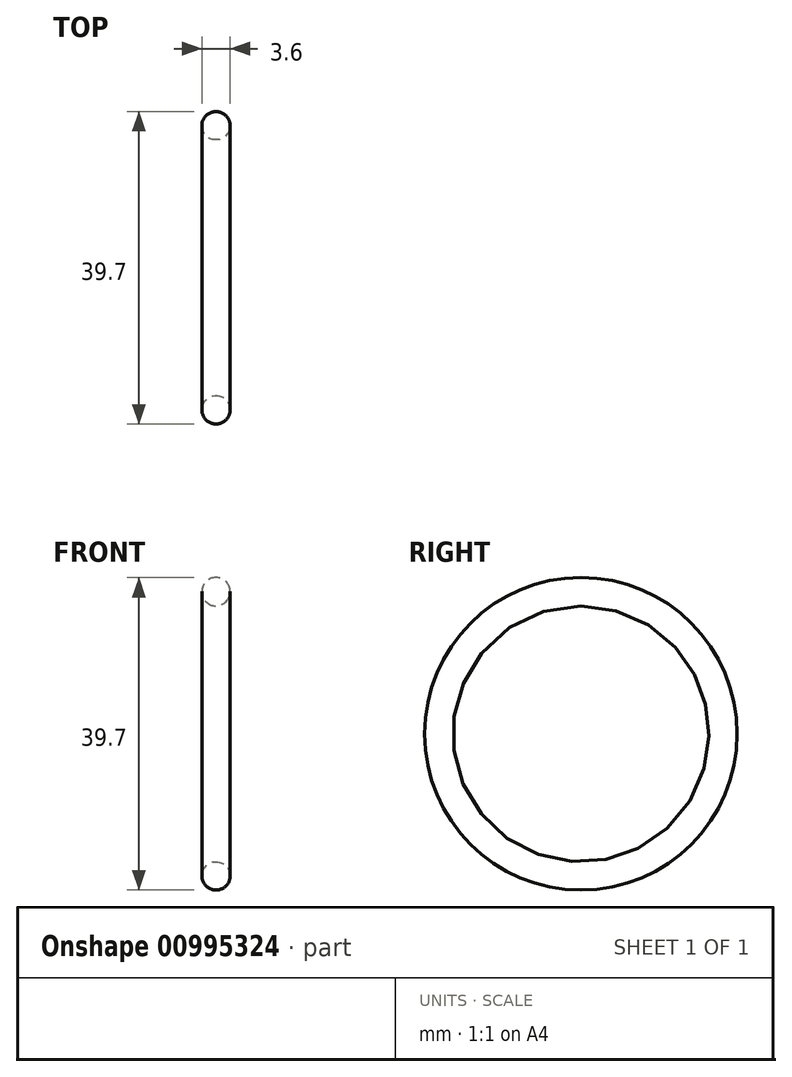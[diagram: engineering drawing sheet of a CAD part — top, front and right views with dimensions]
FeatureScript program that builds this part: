
annotation { "Feature Type Name" : "Feature", "Feature Type Description" : "" }
export const myFeature = defineFeature(function(context is Context, id is Id, definition is map)
    precondition{}
    {
        {
            var Q0;
            Q0=qCreatedBy(makeId("Front.planeOp"),FACE);
            var sketch = newSketch(context, id + "F0", { "sketchPlane" : qUnion([Q0])});
            skCircle(sketch, "E0", {"center": v(0, 0) * mm, "radius": 1.8 * mm});
            skLineSegment(sketch, "E1", {"start": v(-17.69, -18.05) * mm, "end": v(20.89, -18.05) * mm, "construction": true});
            skSolve(sketch);
        }
        {
            var Q0;
            Q0=makeQuery(id+"F0.imprint","IMPRINT",FACE,{"disambiguationData":[TD([[makeQuery(id+"F0.imprint","IMPRINT",EDGE,{"derivedFrom":sQuery(id+"F0.wireOp",EDGE,"E0")}),1.0]])]});
            var Q1;
            Q1=sQuery(id+"F0.wireOp",EDGE,"E1");
            revolve(context, id + "F1", {"surfaceOperationType" : NewSurfaceOperationType.NEW, "entities" : qUnion([Q0]), "axis" : qUnion([Q1]), "revolveType" : RevolveType.FULL});
        }
    });
